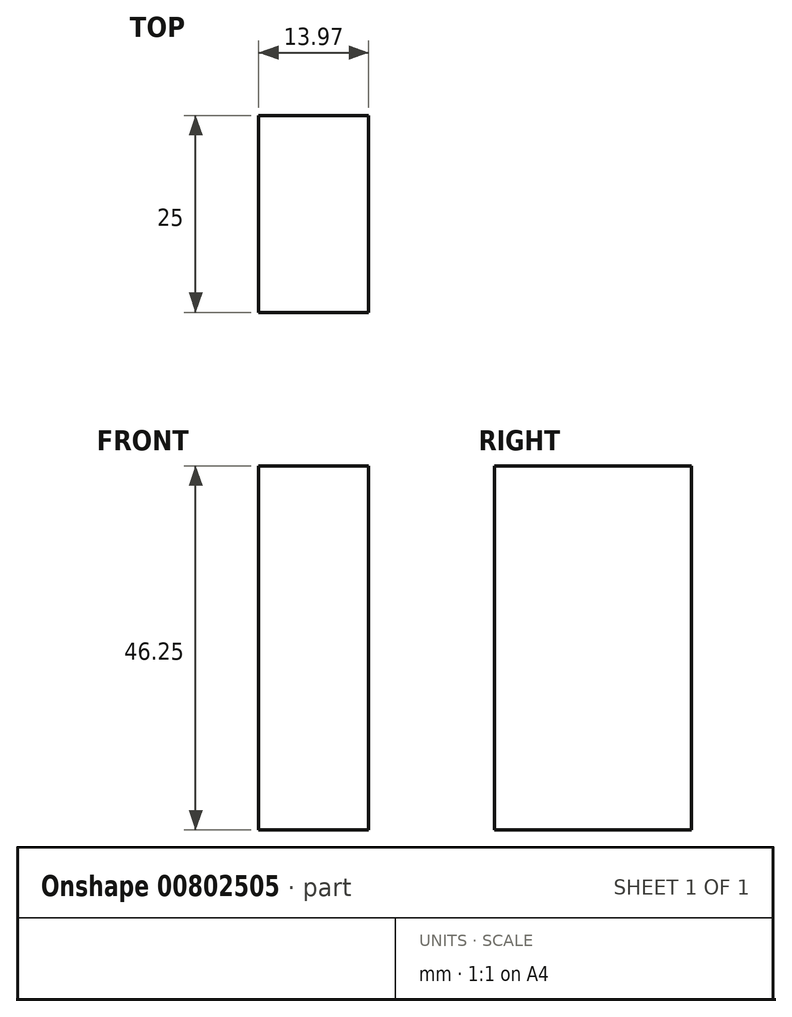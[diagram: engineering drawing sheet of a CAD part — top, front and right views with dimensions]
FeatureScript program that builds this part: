
annotation { "Feature Type Name" : "Feature", "Feature Type Description" : "" }
export const myFeature = defineFeature(function(context is Context, id is Id, definition is map)
    precondition{}
    {
        {
            var Q0;
            Q0=qCreatedBy(makeId("Front.planeOp"),FACE);
            var sketch = newSketch(context, id + "F0", { "sketchPlane" : qUnion([Q0])});
            skLineSegment(sketch, "E0.bottom", {"start": v(-18.3, 23.9) * mm, "end": v(-4.33, 23.9) * mm});
            skLineSegment(sketch, "E0.top", {"start": v(-18.3, 70.15) * mm, "end": v(-4.33, 70.15) * mm});
            skLineSegment(sketch, "E0.left", {"start": v(-18.3, 23.9) * mm, "end": v(-18.3, 70.15) * mm});
            skLineSegment(sketch, "E0.right", {"start": v(-4.33, 23.9) * mm, "end": v(-4.33, 70.15) * mm});
            skSolve(sketch);
        }
        {
            var Q0;
            Q0=makeQuery(id+"F0.imprint","IMPRINT",FACE,{"disambiguationData":[TD([[makeQuery(id+"F0.imprint","IMPRINT",EDGE,{"derivedFrom":sQuery(id+"F0.wireOp",EDGE,"E0.bottom")}),1.0]])]});
            extrude(context, id + "F1", {"entities" : qUnion([Q0]), "depth" : 25 * mm, "offsetDistance" : 25 * mm});
        }
    });
